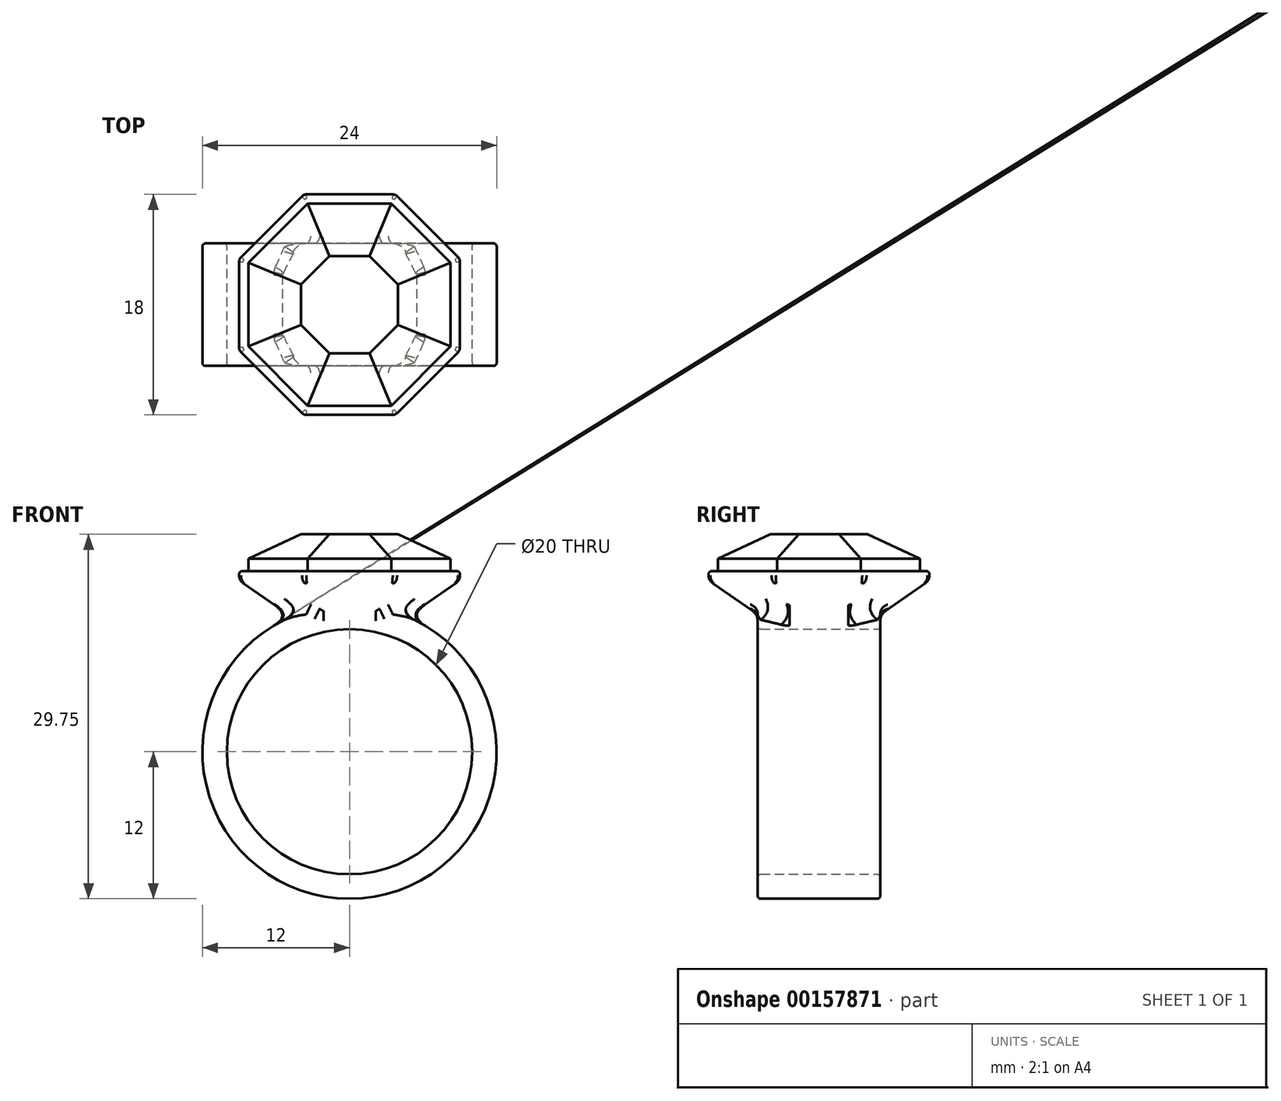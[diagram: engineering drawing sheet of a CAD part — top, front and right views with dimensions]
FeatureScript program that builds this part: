
annotation { "Feature Type Name" : "Feature", "Feature Type Description" : "" }
export const myFeature = defineFeature(function(context is Context, id is Id, definition is map)
    precondition{}
    {
        {
            var Q0;
            Q0=qCreatedBy(makeId("Front.planeOp"),FACE);
            var sketch = newSketch(context, id + "F0", { "sketchPlane" : qUnion([Q0])});
            skCircle(sketch, "E0", {"center": v(0, 0) * mm, "radius": 10 * mm});
            skCircle(sketch, "E1.0", {"center": v(0, 0) * mm, "radius": 12 * mm});
            skSolve(sketch);
        }
        {
            var Q0;
            Q0 = qSketchRegion(id + "F0", true);
            extrude(context, id + "F1", {"entities" : qUnion([Q0]), "endBound" : BoundingType.SYMMETRIC, "depth" : 10 * mm});
        }
        {
            var Q0;
            Q0=qCreatedBy(makeId("Top.planeOp"),FACE);
            cPlane(context, id + "F2", {"entities" : qUnion([Q0]), "cplaneType" : CPlaneType.OFFSET, "offset" : 14 * mm, "width" : 150 * mm, "height" : 150 * mm});
        }
        {
            var Q0;
            Q0=qCreatedBy(id+"F2.planeOp",FACE);
            var sketch = newSketch(context, id + "F3", { "sketchPlane" : qUnion([Q0])});
            skCircle(sketch, "E2.cCircle", {"center": v(0, 0) * mm, "radius": 9 * mm, "construction": true});
            skLineSegment(sketch, "E2.0", {"start": v(9, 3.73) * mm, "end": v(9, -3.73) * mm});
            skLineSegment(sketch, "E2.1", {"start": v(9, -3.73) * mm, "end": v(3.73, -9) * mm});
            skLineSegment(sketch, "E2.2", {"start": v(3.73, -9) * mm, "end": v(-3.73, -9) * mm});
            skLineSegment(sketch, "E2.3", {"start": v(-3.73, -9) * mm, "end": v(-9, -3.73) * mm});
            skLineSegment(sketch, "E2.4", {"start": v(-9, -3.73) * mm, "end": v(-9, 3.73) * mm});
            skLineSegment(sketch, "E2.5", {"start": v(-9, 3.73) * mm, "end": v(-3.73, 9) * mm});
            skLineSegment(sketch, "E2.6", {"start": v(-3.73, 9) * mm, "end": v(3.73, 9) * mm});
            skLineSegment(sketch, "E2.7", {"start": v(3.73, 9) * mm, "end": v(9, 3.73) * mm});
            skPoint(sketch, "E2.0.midPoint", {"position": v(9, 0) * mm});
            skSolve(sketch);
        }
        {
            var Q0;
            Q0=makeQuery(id+"F3.imprint","IMPRINT",FACE,{"disambiguationData":[TD([[makeQuery(id+"F3.imprint","IMPRINT",EDGE,{"derivedFrom":sQuery(id+"F3.wireOp",EDGE,"E2.0")}),-1.0]])]});
            var Q1;
            Q1=makeQuery(id+"F1.opExtrude","SWEPT_FACE",FACE,{"disambiguationData":[OSD([sQuery(id+"F0.wireOp",EDGE,"E0")])]});
            extrude(context, id + "F4", {"entities" : qUnion([Q0]), "operationType" : NewBodyOperationType.ADD, "endBound" : BoundingType.UP_TO_SURFACE, "oppositeDirection" : true, "endBoundEntityFace" : qUnion([Q1]), "depth" : 25 * mm, "hasDraft" : true, "draftAngle" : 55 * degree, "draftPullDirection" : true});
        }
        {
            var Q0;
            Q0=makeQuery(id+"F4.opExtrude","CAP_FACE",FACE,{"disambiguationData":[OSD([sQuery(id+"F3.wireOp",EDGE,"E2.0"),sQuery(id+"F3.wireOp",EDGE,"E2.1"),sQuery(id+"F3.wireOp",EDGE,"E2.2"),sQuery(id+"F3.wireOp",EDGE,"E2.3"),sQuery(id+"F3.wireOp",EDGE,"E2.4"),sQuery(id+"F3.wireOp",EDGE,"E2.5"),sQuery(id+"F3.wireOp",EDGE,"E2.6"),sQuery(id+"F3.wireOp",EDGE,"E2.7")])],"isStart":true});
            extrude(context, id + "F5", {"entities" : qUnion([Q0]), "operationType" : NewBodyOperationType.ADD, "depth" : 0.75 * mm});
        }
        {
            var Q0;
            Q0=makeQuery(id+"F5.opExtrude","CAP_FACE",FACE,{"disambiguationData":[OSD([sQuery(id+"F3.wireOp",EDGE,"E2.0"),sQuery(id+"F3.wireOp",EDGE,"E2.1"),sQuery(id+"F3.wireOp",EDGE,"E2.2"),sQuery(id+"F3.wireOp",EDGE,"E2.3"),sQuery(id+"F3.wireOp",EDGE,"E2.4"),sQuery(id+"F3.wireOp",EDGE,"E2.5"),sQuery(id+"F3.wireOp",EDGE,"E2.6"),sQuery(id+"F3.wireOp",EDGE,"E2.7")])],"isStart":false});
            var sketch = newSketch(context, id + "F6", { "sketchPlane" : qUnion([Q0])});
            skLineSegment(sketch, "E3.0", {"start": v(3.42, 8.25) * mm, "end": v(8.25, 3.42) * mm});
            skLineSegment(sketch, "E3.1", {"start": v(-3.42, 8.25) * mm, "end": v(3.42, 8.25) * mm});
            skLineSegment(sketch, "E3.2", {"start": v(8.25, 3.42) * mm, "end": v(8.25, -3.42) * mm});
            skLineSegment(sketch, "E3.3", {"start": v(-8.25, 3.42) * mm, "end": v(-3.42, 8.25) * mm});
            skLineSegment(sketch, "E3.4", {"start": v(8.25, -3.42) * mm, "end": v(3.42, -8.25) * mm});
            skLineSegment(sketch, "E3.5", {"start": v(3.42, -8.25) * mm, "end": v(-3.42, -8.25) * mm});
            skLineSegment(sketch, "E3.6", {"start": v(-3.42, -8.25) * mm, "end": v(-8.25, -3.42) * mm});
            skLineSegment(sketch, "E3.7", {"start": v(-8.25, -3.42) * mm, "end": v(-8.25, 3.42) * mm});
            skSolve(sketch);
        }
        {
            var Q0;
            Q0=makeQuery(id+"F6.imprint","IMPRINT",FACE,{"disambiguationData":[TD([[makeQuery(id+"F6.imprint","IMPRINT",EDGE,{"derivedFrom":sQuery(id+"F6.wireOp",EDGE,"E3.0")}),-1.0]])]});
            extrude(context, id + "F7", {"entities" : qUnion([Q0]), "depth" : 3 * mm});
        }
        {
            var Q0;
            Q0=makeQuery(id+"F7.opExtrude","CAP_EDGE",EDGE,{"disambiguationData":[OSD([sQuery(id+"F6.wireOp",EDGE,"E3.5")])],"isStart":false});
            var Q1;
            Q1=makeQuery(id+"F7.opExtrude","CAP_EDGE",EDGE,{"disambiguationData":[OSD([sQuery(id+"F6.wireOp",EDGE,"E3.4")])],"isStart":false});
            var Q2;
            Q2=makeQuery(id+"F7.opExtrude","CAP_EDGE",EDGE,{"disambiguationData":[OSD([sQuery(id+"F6.wireOp",EDGE,"E3.2")])],"isStart":false});
            var Q3;
            Q3=makeQuery(id+"F7.opExtrude","CAP_EDGE",EDGE,{"disambiguationData":[OSD([sQuery(id+"F6.wireOp",EDGE,"E3.0")])],"isStart":false});
            var Q4;
            Q4=makeQuery(id+"F7.opExtrude","CAP_EDGE",EDGE,{"disambiguationData":[OSD([sQuery(id+"F6.wireOp",EDGE,"E3.1")])],"isStart":false});
            var Q5;
            Q5=makeQuery(id+"F7.opExtrude","CAP_EDGE",EDGE,{"disambiguationData":[OSD([sQuery(id+"F6.wireOp",EDGE,"E3.3")])],"isStart":false});
            var Q6;
            Q6=makeQuery(id+"F7.opExtrude","CAP_EDGE",EDGE,{"disambiguationData":[OSD([sQuery(id+"F6.wireOp",EDGE,"E3.7")])],"isStart":false});
            var Q7;
            Q7=makeQuery(id+"F7.opExtrude","CAP_EDGE",EDGE,{"disambiguationData":[OSD([sQuery(id+"F6.wireOp",EDGE,"E3.6")])],"isStart":false});
            chamfer(context, id + "F8", {"entities" : qUnion([Q0, Q1, Q2, Q3, Q4, Q5, Q6, Q7]), "chamferType" : ChamferType.OFFSET_ANGLE, "width" : 2 * mm, "oppositeDirection" : false, "angle" : 65 * degree, "tangentPropagation" : true});
        }
        {
            var Q0;
            {var subQ0=sQuery(id+"F3.wireOp",EDGE,"E2.2");Q0=makeQuery(id+"F5.boolean.opBoolean","MERGE",EDGE,{"derivedFrom":[makeQuery(id+"F4.opExtrude","CAP_EDGE",EDGE,{"disambiguationData":[OSD([subQ0])],"isStart":true}),makeQuery(id+"F5.opExtrude","CAP_EDGE",EDGE,{"disambiguationData":[OSD([subQ0])],"isStart":true})]});}
            var Q1;
            {var subQ0=sQuery(id+"F3.wireOp",EDGE,"E2.1");Q1=makeQuery(id+"F5.boolean.opBoolean","MERGE",EDGE,{"derivedFrom":[makeQuery(id+"F4.opExtrude","CAP_EDGE",EDGE,{"disambiguationData":[OSD([subQ0])],"isStart":true}),makeQuery(id+"F5.opExtrude","CAP_EDGE",EDGE,{"disambiguationData":[OSD([subQ0])],"isStart":true})]});}
            var Q2;
            {var subQ0=sQuery(id+"F3.wireOp",EDGE,"E2.0");Q2=makeQuery(id+"F5.boolean.opBoolean","MERGE",EDGE,{"derivedFrom":[makeQuery(id+"F4.opExtrude","CAP_EDGE",EDGE,{"disambiguationData":[OSD([subQ0])],"isStart":true}),makeQuery(id+"F5.opExtrude","CAP_EDGE",EDGE,{"disambiguationData":[OSD([subQ0])],"isStart":true})]});}
            var Q3;
            {var subQ0=sQuery(id+"F3.wireOp",EDGE,"E2.3");Q3=makeQuery(id+"F5.boolean.opBoolean","MERGE",EDGE,{"derivedFrom":[makeQuery(id+"F4.opExtrude","CAP_EDGE",EDGE,{"disambiguationData":[OSD([subQ0])],"isStart":true}),makeQuery(id+"F5.opExtrude","CAP_EDGE",EDGE,{"disambiguationData":[OSD([subQ0])],"isStart":true})]});}
            var Q4;
            {var subQ0=sQuery(id+"F3.wireOp",EDGE,"E2.7");Q4=makeQuery(id+"F5.boolean.opBoolean","MERGE",EDGE,{"derivedFrom":[makeQuery(id+"F4.opExtrude","CAP_EDGE",EDGE,{"disambiguationData":[OSD([subQ0])],"isStart":true}),makeQuery(id+"F5.opExtrude","CAP_EDGE",EDGE,{"disambiguationData":[OSD([subQ0])],"isStart":true})]});}
            var Q5;
            {var subQ0=sQuery(id+"F3.wireOp",EDGE,"E2.6");Q5=makeQuery(id+"F5.boolean.opBoolean","MERGE",EDGE,{"derivedFrom":[makeQuery(id+"F4.opExtrude","CAP_EDGE",EDGE,{"disambiguationData":[OSD([subQ0])],"isStart":true}),makeQuery(id+"F5.opExtrude","CAP_EDGE",EDGE,{"disambiguationData":[OSD([subQ0])],"isStart":true})]});}
            var Q6;
            {var subQ0=sQuery(id+"F3.wireOp",EDGE,"E2.5");Q6=makeQuery(id+"F5.boolean.opBoolean","MERGE",EDGE,{"derivedFrom":[makeQuery(id+"F4.opExtrude","CAP_EDGE",EDGE,{"disambiguationData":[OSD([subQ0])],"isStart":true}),makeQuery(id+"F5.opExtrude","CAP_EDGE",EDGE,{"disambiguationData":[OSD([subQ0])],"isStart":true})]});}
            var Q7;
            {var subQ0=sQuery(id+"F3.wireOp",EDGE,"E2.4");Q7=makeQuery(id+"F5.boolean.opBoolean","MERGE",EDGE,{"derivedFrom":[makeQuery(id+"F4.opExtrude","CAP_EDGE",EDGE,{"disambiguationData":[OSD([subQ0])],"isStart":true}),makeQuery(id+"F5.opExtrude","CAP_EDGE",EDGE,{"disambiguationData":[OSD([subQ0])],"isStart":true})]});}
            fillet(context, id + "F9", {"entities" : qUnion([Q0, Q1, Q2, Q3, Q4, Q5, Q6, Q7]), "radius" : 0.75 * mm, "tangentPropagation" : true, "rho" : 0.5, "crossSection" : FilletCrossSection.CONIC, "allowEdgeOverflow" : false});
        }
        {
            var Q0;
            Q0=makeQuery(id+"F1.opExtrude","CAP_EDGE",EDGE,{"disambiguationData":[OSD([sQuery(id+"F0.wireOp",EDGE,"E1.0")])],"isStart":false});
            var Q1;
            Q1=makeQuery(id+"F1.opExtrude","CAP_EDGE",EDGE,{"disambiguationData":[OSD([sQuery(id+"F0.wireOp",EDGE,"E1.0")])],"isStart":true});
            var Q2;
            Q2=makeQuery(id+"F1.opExtrude","SWEPT_FACE",FACE,{"disambiguationData":[OSD([sQuery(id+"F0.wireOp",EDGE,"E0")])]});
            fillet(context, id + "F10", {"entities" : qUnion([Q0, Q1, Q2]), "radius" : 0.25 * mm, "tangentPropagation" : true, "allowEdgeOverflow" : false});
        }
        {
            var Q0;
            Q0=makeQuery(id+"F4.opExtrude","SWEPT_EDGE",EDGE,{"disambiguationData":[OSD([sQuery(id+"F3.wireOp",EDGE,"E2.1"),sQuery(id+"F3.wireOp",EDGE,"E2.2")])]});
            var Q1;
            Q1=makeQuery(id+"F4.opExtrude","SWEPT_EDGE",EDGE,{"disambiguationData":[OSD([sQuery(id+"F3.wireOp",EDGE,"E2.0"),sQuery(id+"F3.wireOp",EDGE,"E2.1")])]});
            var Q2;
            Q2=makeQuery(id+"F4.opExtrude","SWEPT_EDGE",EDGE,{"disambiguationData":[OSD([sQuery(id+"F3.wireOp",EDGE,"E2.0"),sQuery(id+"F3.wireOp",EDGE,"E2.7")])]});
            var Q3;
            Q3=makeQuery(id+"F4.opExtrude","SWEPT_EDGE",EDGE,{"disambiguationData":[OSD([sQuery(id+"F3.wireOp",EDGE,"E2.2"),sQuery(id+"F3.wireOp",EDGE,"E2.3")])]});
            var Q4;
            Q4=makeQuery(id+"F4.opExtrude","SWEPT_EDGE",EDGE,{"disambiguationData":[OSD([sQuery(id+"F3.wireOp",EDGE,"E2.3"),sQuery(id+"F3.wireOp",EDGE,"E2.4")])]});
            var Q5;
            Q5=makeQuery(id+"F4.opExtrude","SWEPT_EDGE",EDGE,{"disambiguationData":[OSD([sQuery(id+"F3.wireOp",EDGE,"E2.4"),sQuery(id+"F3.wireOp",EDGE,"E2.5")])]});
            var Q6;
            Q6=makeQuery(id+"F4.opExtrude","SWEPT_EDGE",EDGE,{"disambiguationData":[OSD([sQuery(id+"F3.wireOp",EDGE,"E2.5"),sQuery(id+"F3.wireOp",EDGE,"E2.6")])]});
            var Q7;
            Q7=makeQuery(id+"F4.opExtrude","SWEPT_EDGE",EDGE,{"disambiguationData":[OSD([sQuery(id+"F3.wireOp",EDGE,"E2.6"),sQuery(id+"F3.wireOp",EDGE,"E2.7")])]});
            fillet(context, id + "F11", {"entities" : qUnion([Q0, Q1, Q2, Q3, Q4, Q5, Q6, Q7]), "radius" : 0.5 * mm, "tangentPropagation" : true, "allowEdgeOverflow" : false});
        }
        {
            var Q0;
            Q0=makeQuery(id+"F4.boolean.opBoolean","INTERSECT",EDGE,{"derivedFrom":[makeQuery(id+"F1.opExtrude","SWEPT_FACE",FACE,{"disambiguationData":[OSD([sQuery(id+"F0.wireOp",EDGE,"E1.0")])]}),makeQuery(id+"F4.opExtrude","SWEPT_FACE",FACE,{"disambiguationData":[OSD([sQuery(id+"F3.wireOp",EDGE,"E2.4")])]})]});
            fillet(context, id + "F12", {"entities" : qUnion([Q0]), "radius" : 1 * mm, "tangentPropagation" : true, "rho" : 0.5, "crossSection" : FilletCrossSection.CONIC, "allowEdgeOverflow" : false});
        }
        {
            var Q0;
            Q0=makeQuery(id+"F5.opExtrude","CAP_EDGE",EDGE,{"disambiguationData":[OSD([sQuery(id+"F3.wireOp",EDGE,"E2.2")])],"isStart":false});
            fillet(context, id + "F13", {"entities" : qUnion([Q0]), "radius" : 0.25 * mm, "tangentPropagation" : true, "allowEdgeOverflow" : false});
        }
    });
